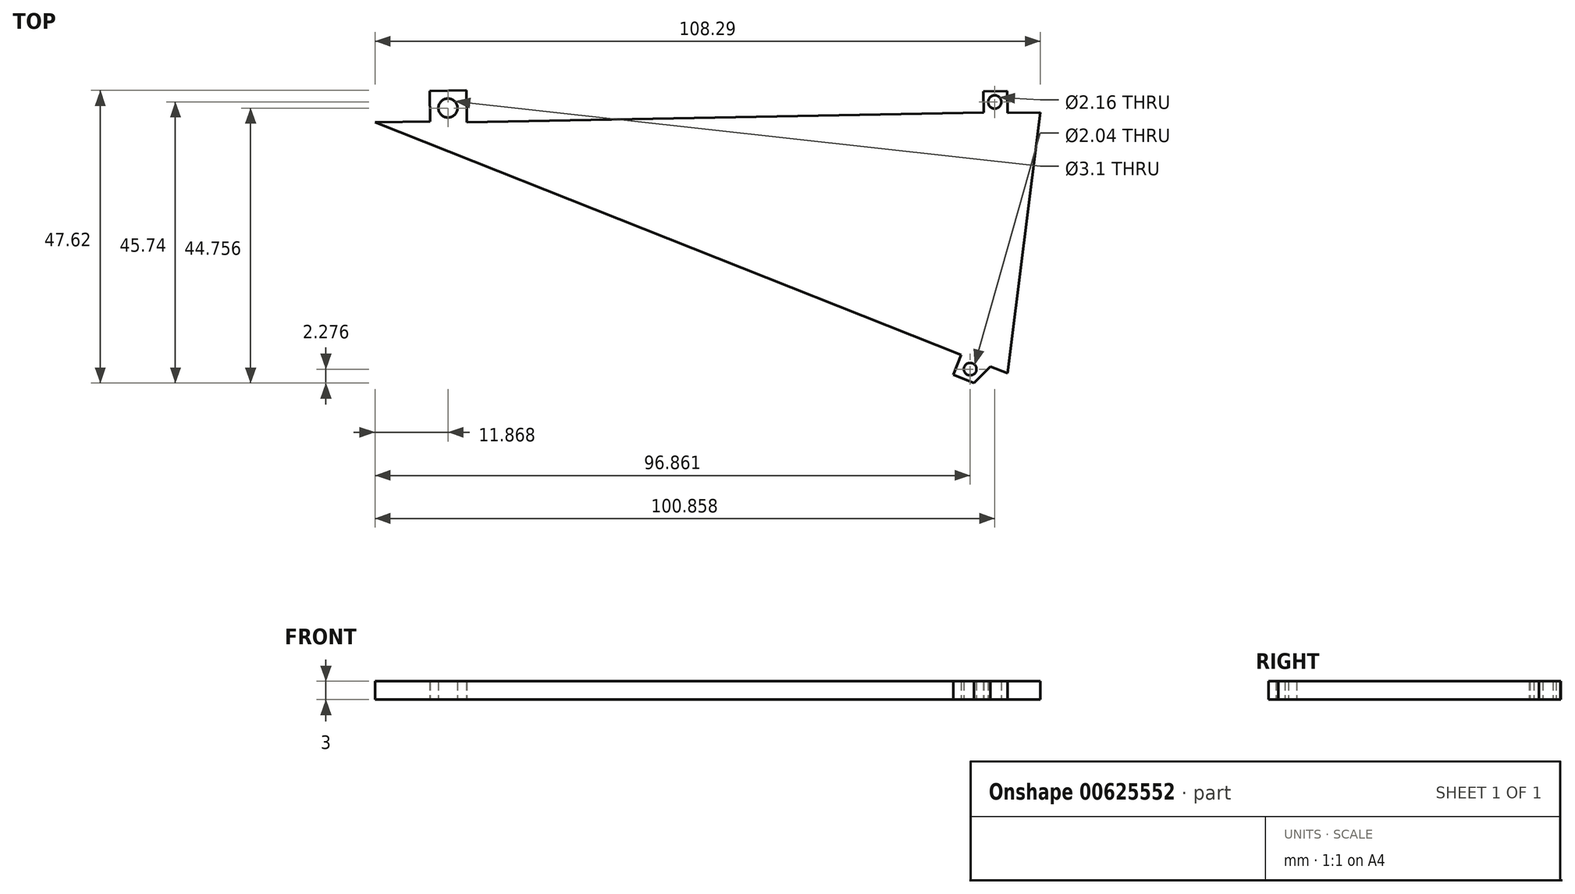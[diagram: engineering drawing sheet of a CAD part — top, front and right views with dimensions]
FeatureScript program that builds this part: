
annotation { "Feature Type Name" : "Feature", "Feature Type Description" : "" }
export const myFeature = defineFeature(function(context is Context, id is Id, definition is map)
    precondition{}
    {
        {
            var Q0;
            Q0=qCreatedBy(makeId("Top.planeOp"),FACE);
            var sketch = newSketch(context, id + "F0", { "sketchPlane" : qUnion([Q0])});
            skLineSegment(sketch, "E0", {"start": v(-53.25, -5.1) * mm, "end": v(42.13, -42.92) * mm});
            skLineSegment(sketch, "E1", {"start": v(49.67, -45.9) * mm, "end": v(55.04, -3.5) * mm});
            skLineSegment(sketch, "E2", {"start": v(55.04, -3.5) * mm, "end": v(49.66, -3.57) * mm});
            skLineSegment(sketch, "E3", {"start": v(-44.3, -4.97) * mm, "end": v(-44.37, 0) * mm});
            skLineSegment(sketch, "E4", {"start": v(-44.37, 0) * mm, "end": v(-38.4, 0.09) * mm});
            skLineSegment(sketch, "E5", {"start": v(-38.4, 0.09) * mm, "end": v(-38.32, -5.1) * mm});
            skLineSegment(sketch, "E6", {"start": v(49.67, -3.8) * mm, "end": v(49.6, 0) * mm});
            skLineSegment(sketch, "E7", {"start": v(49.6, 0) * mm, "end": v(45.74, -0.06) * mm});
            skLineSegment(sketch, "E8", {"start": v(45.74, -0.06) * mm, "end": v(45.8, -3.5) * mm});
            skLineSegment(sketch, "E9", {"start": v(42.13, -42.92) * mm, "end": v(40.84, -46.17) * mm});
            skLineSegment(sketch, "E10", {"start": v(40.84, -46.17) * mm, "end": v(44.26, -47.53) * mm});
            skLineSegment(sketch, "E11", {"start": v(44.26, -47.53) * mm, "end": v(46.92, -44.82) * mm});
            skCircle(sketch, "E12", {"center": v(-41.38, -2.77) * mm, "radius": 1.55 * mm});
            skPoint(sketch, "E12.centerSnap0", {"position": v(-41.38, 0.04) * mm});
            skCircle(sketch, "E13", {"center": v(47.6, -1.79) * mm, "radius": 1.08 * mm});
            skCircle(sketch, "E14", {"center": v(43.61, -45.25) * mm, "radius": 1.02 * mm});
            skLineSegment(sketch, "E15.trimOffspring", {"start": v(-44.3, -4.97) * mm, "end": v(-53.25, -5.1) * mm});
            skLineSegment(sketch, "E16.trimOffspring", {"start": v(46.92, -44.82) * mm, "end": v(49.67, -45.9) * mm});
            skLineSegment(sketch, "E17", {"start": v(-38.32, -5.1) * mm, "end": v(45.8, -3.5) * mm});
            skSolve(sketch);
        }
        {
            var Q0;
            Q0 = qSketchRegion(id + "F0", true);
            extrude(context, id + "F1", {"entities" : qUnion([Q0]), "depth" : 3 * mm, "offsetDistance" : 25 * mm});
        }
    });
